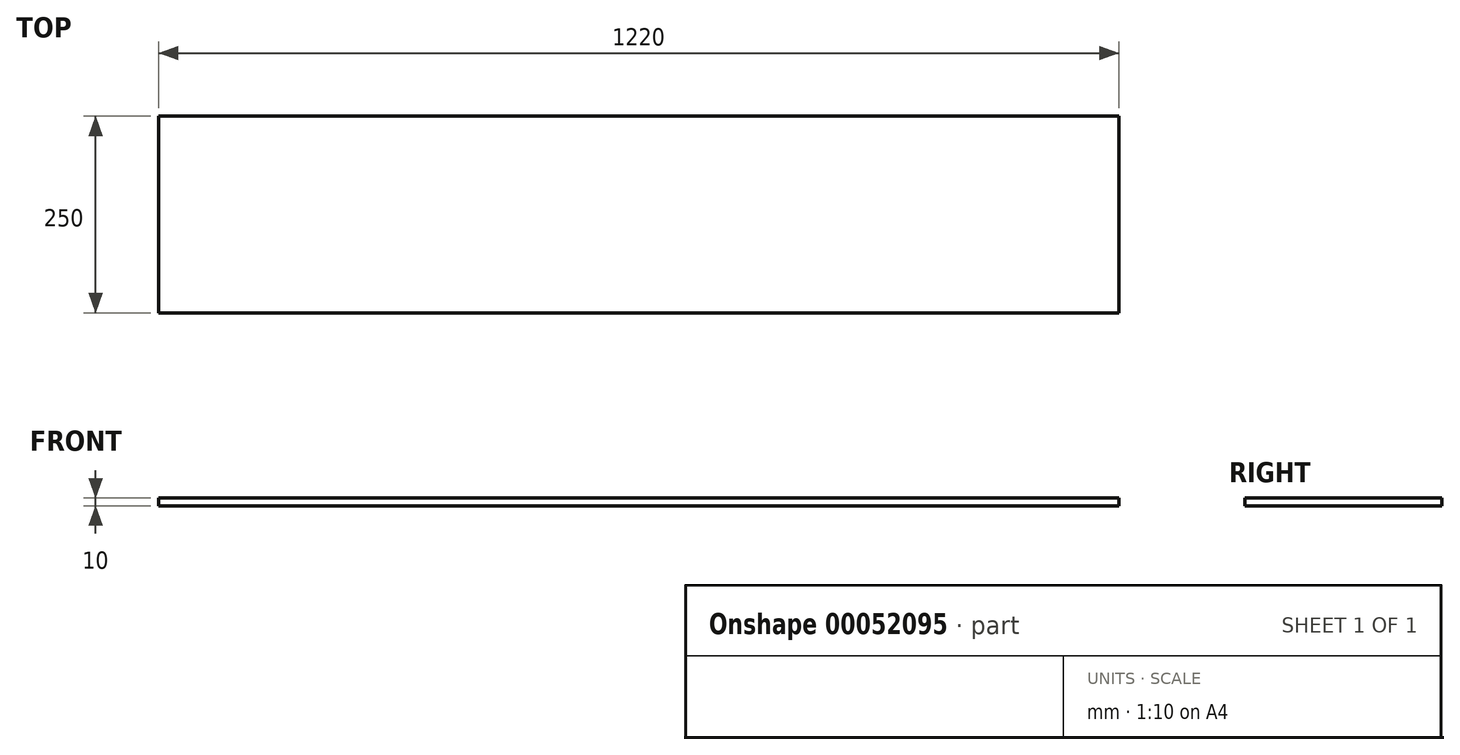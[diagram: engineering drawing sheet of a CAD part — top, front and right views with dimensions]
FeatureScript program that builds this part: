
annotation { "Feature Type Name" : "Feature", "Feature Type Description" : "" }
export const myFeature = defineFeature(function(context is Context, id is Id, definition is map)
    precondition{}
    {
        {
            var Q0;
            Q0=qCreatedBy(makeId("Top.planeOp"),FACE);
            var sketch = newSketch(context, id + "F0", { "sketchPlane" : qUnion([Q0])});
            skLineSegment(sketch, "E0.bottom", {"start": v(0, 0) * mm, "end": v(1220, 0) * mm});
            skLineSegment(sketch, "E0.top", {"start": v(0, 250) * mm, "end": v(1220, 250) * mm});
            skLineSegment(sketch, "E0.left", {"start": v(0, 0) * mm, "end": v(0, 250) * mm});
            skLineSegment(sketch, "E0.right", {"start": v(1220, 0) * mm, "end": v(1220, 250) * mm});
            skSolve(sketch);
        }
        {
            var Q0;
            Q0=makeQuery(id+"F0.imprint","IMPRINT",FACE,{"disambiguationData":[TD([[makeQuery(id+"F0.imprint","IMPRINT",EDGE,{"derivedFrom":sQuery(id+"F0.wireOp",EDGE,"E0.bottom")}),1.0]])]});
            extrude(context, id + "F1", {"entities" : qUnion([Q0]), "depth" : 10 * mm});
        }
    });
